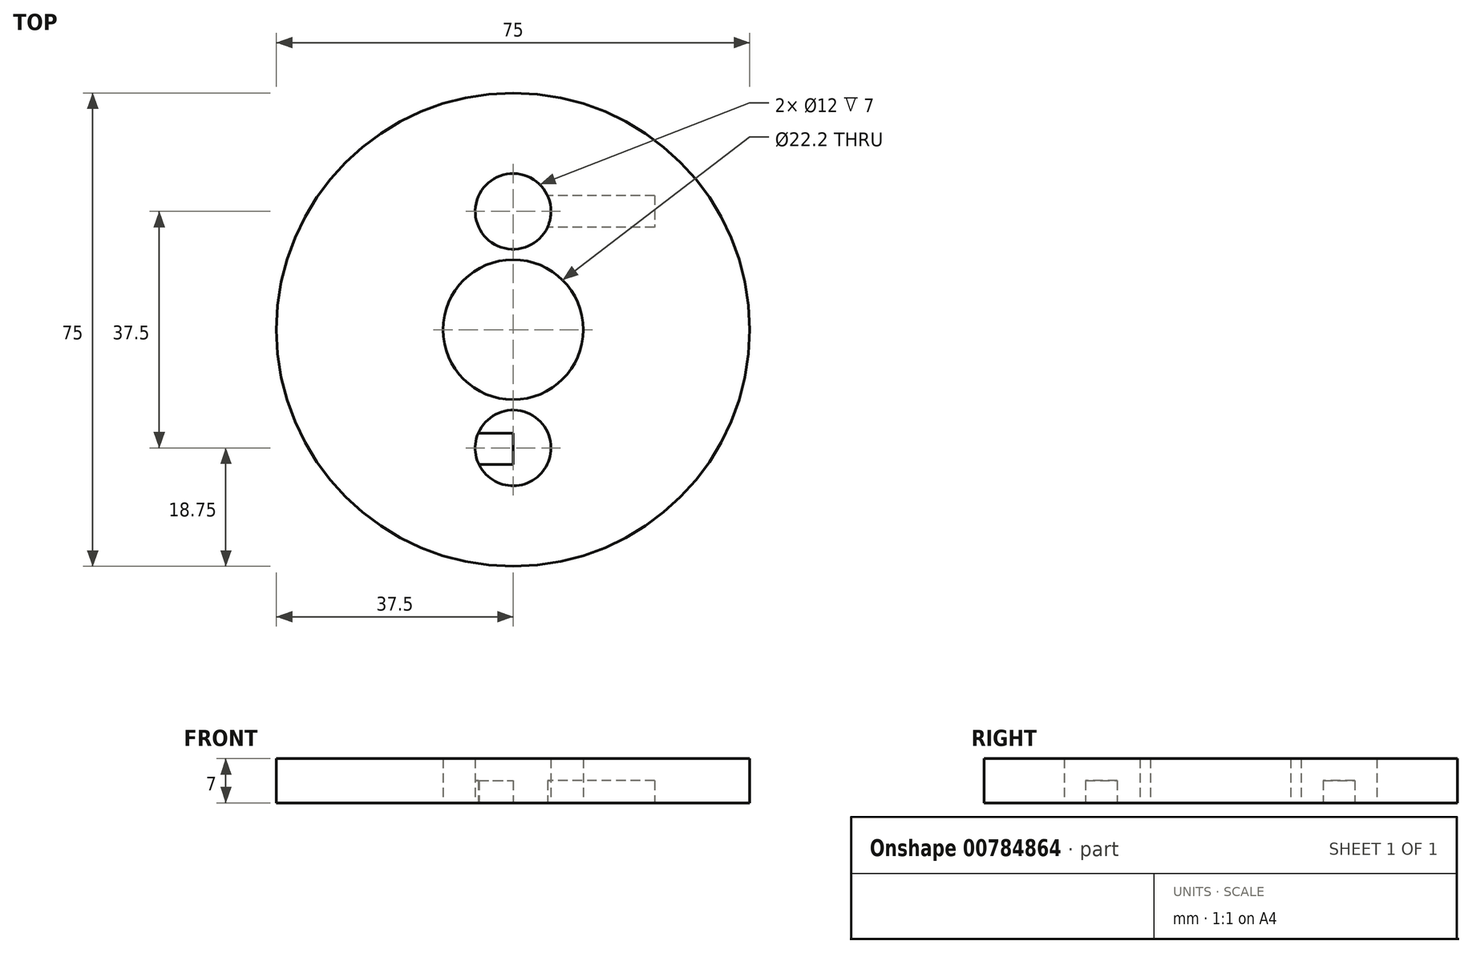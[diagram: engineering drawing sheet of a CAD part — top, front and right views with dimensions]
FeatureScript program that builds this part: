
annotation { "Feature Type Name" : "Feature", "Feature Type Description" : "" }
export const myFeature = defineFeature(function(context is Context, id is Id, definition is map)
    precondition{}
    {
        {
            var Q0;
            Q0=qCreatedBy(makeId("Top.planeOp"),FACE);
            var sketch = newSketch(context, id + "F0", { "sketchPlane" : qUnion([Q0])});
            skCircle(sketch, "E0", {"center": v(0, 0) * mm, "radius": 37.5 * mm});
            skArc(sketch, "E1", {"start": v(0, 0) * mm, "mid": v(18.75, 18.75) * mm, "end": v(0, 37.5) * mm});
            skArc(sketch, "E2.1.0", {"start": v(0, 0) * mm, "mid": v(-18.75, -18.75) * mm, "end": v(0, -37.5) * mm});
            skCircle(sketch, "E3", {"center": v(0, 0) * mm, "radius": 11.1 * mm});
            skCircle(sketch, "E4", {"center": v(0, 18.75) * mm, "radius": 6 * mm});
            skCircle(sketch, "E5.MirrorC", {"center": v(0, -18.75) * mm, "radius": 6 * mm});
            skSolve(sketch);
        }
        {
            var Q0;
            Q0=makeQuery(id+"F0.imprint","IMPRINT",FACE,{"disambiguationData":[TD([[makeQuery(id+"F0.imprint","IMPRINT",EDGE,{"derivedFrom":sQuery(id+"F0.wireOp",EDGE,"E4")}),-1.0]])]});
            var Q1;
            Q1=makeQuery(id+"F0.imprint","IMPRINT",FACE,{"disambiguationData":[TD([[makeQuery(id+"F0.imprint","IMPRINT",EDGE,{"derivedFrom":sQuery(id+"F0.wireOp",EDGE,"E5.MirrorC")}),-1.0]])]});
            extrude(context, id + "F1", {"entities" : qUnion([Q0, Q1]), "depth" : 7 * mm, "offsetDistance" : 25 * mm});
        }
        {
            var Q0;
            Q0=qCreatedBy(makeId("Top.planeOp"),FACE);
            var sketch = newSketch(context, id + "F2", { "sketchPlane" : qUnion([Q0])});
            skLineSegment(sketch, "E6", {"start": v(0, -18.88) * mm, "end": v(-18.75, -18.88) * mm, "construction": true});
            skLineSegment(sketch, "E7.bottom", {"start": v(-18.75, -21.38) * mm, "end": v(0, -21.38) * mm});
            skLineSegment(sketch, "E7.top", {"start": v(-18.75, -16.38) * mm, "end": v(0, -16.38) * mm});
            skLineSegment(sketch, "E7.left", {"start": v(-18.75, -21.38) * mm, "end": v(-18.75, -16.38) * mm});
            skLineSegment(sketch, "E7.right", {"start": v(0, -21.38) * mm, "end": v(0, -16.38) * mm});
            skPoint(sketch, "E7.middle", {"position": v(-9.37, -18.88) * mm});
            skSolve(sketch);
        }
        {
            var Q0;
            Q0=makeQuery(id+"F2.imprint","IMPRINT",FACE,{"disambiguationData":[TD([[makeQuery(id+"F2.imprint","IMPRINT",EDGE,{"derivedFrom":sQuery(id+"F2.wireOp",EDGE,"E7.bottom")}),1.0]])]});
            extrude(context, id + "F3", {"entities" : qUnion([Q0]), "operationType" : NewBodyOperationType.ADD, "depth" : 3.5 * mm, "offsetDistance" : 25 * mm});
        }
        {
            var Q0;
            Q0=qCreatedBy(makeId("Top.planeOp"),FACE);
            var sketch = newSketch(context, id + "F4", { "sketchPlane" : qUnion([Q0])});
            skLineSegment(sketch, "E8.bottom", {"start": v(22.43, 21.25) * mm, "end": v(0, 21.25) * mm});
            skLineSegment(sketch, "E8.top", {"start": v(22.43, 16.25) * mm, "end": v(0, 16.25) * mm});
            skLineSegment(sketch, "E8.left", {"start": v(22.43, 21.25) * mm, "end": v(22.43, 16.25) * mm});
            skLineSegment(sketch, "E8.right", {"start": v(0, 21.25) * mm, "end": v(0, 16.25) * mm});
            skPoint(sketch, "E8.middle", {"position": v(11.22, 18.75) * mm});
            skSolve(sketch);
        }
        {
            var Q0;
            Q0 = qSketchRegion(id + "F4", true);
            extrude(context, id + "F5", {"entities" : qUnion([Q0]), "operationType" : NewBodyOperationType.REMOVE, "depth" : 3.5 * mm, "offsetDistance" : 25 * mm});
        }
    });
